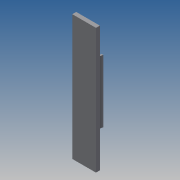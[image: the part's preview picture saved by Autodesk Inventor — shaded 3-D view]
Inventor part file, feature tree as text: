
AUTODESK INVENTOR PART (.ipt)
format: ipt  version: 2014 SP1 (Build 180222100, 222)  size: 84,992 bytes
history: native  units: in
note: dims shown in document units (in); Inventor stores cm internally (conversion verified against a paired STEP export)
features: sketch x3, extrude x2, plane x1
ambient origin geometry x8: Origin, YZ Plane, XZ Plane, XY Plane, X Axis, Y Axis, Z Axis, Center Point
bodies: Solid1 (feature_tree)
feature tree (6):
  extrude  "Extrusion1"  Depth=0.05in
  sketch  "Sketch2"  dims[d2=2.0in d3=0.0in d4=4.0in]
  plane  "Work Plane1"
  extrude  "Extrusion2"  Depth=4.0in
  sketch  "Sketch1"  dims[d0=0.5in d1=0.05in]
  sketch  "Sketch3"  dims[d5=0.125in d6=0.0in]
